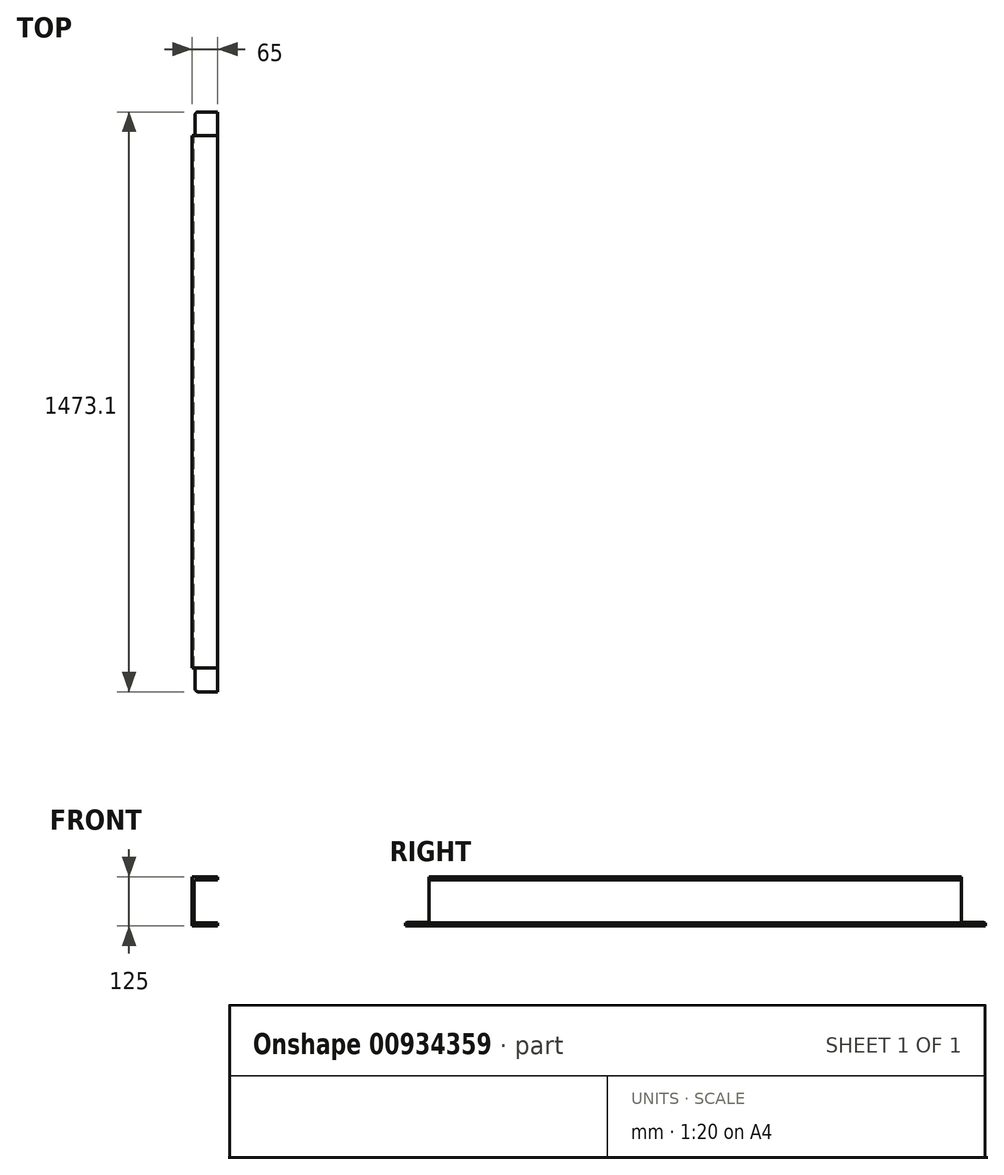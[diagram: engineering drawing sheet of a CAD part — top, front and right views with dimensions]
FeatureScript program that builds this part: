
annotation { "Feature Type Name" : "Feature", "Feature Type Description" : "" }
export const myFeature = defineFeature(function(context is Context, id is Id, definition is map)
    precondition{}
    {
        {
            var Q0;
            Q0=qCreatedBy(makeId("Front.planeOp"),FACE);
            var sketch = newSketch(context, id + "F0", { "sketchPlane" : qUnion([Q0])});
            skLineSegment(sketch, "E0", {"start": v(-25.17, -62.5) * mm, "end": v(-25.17, 62.5) * mm});
            skLineSegment(sketch, "E1", {"start": v(-25.17, 62.5) * mm, "end": v(39.83, 62.5) * mm});
            skLineSegment(sketch, "E2", {"start": v(39.83, 62.5) * mm, "end": v(39.83, 55) * mm});
            skLineSegment(sketch, "E3", {"start": v(39.83, 55) * mm, "end": v(-12.47, 55) * mm});
            skLineSegment(sketch, "E4", {"start": v(-25.17, -62.5) * mm, "end": v(39.83, -62.5) * mm});
            skLineSegment(sketch, "E5", {"start": v(39.83, -62.5) * mm, "end": v(39.83, -55) * mm});
            skLineSegment(sketch, "E6", {"start": v(39.83, -55) * mm, "end": v(-12.47, -55) * mm});
            skLineSegment(sketch, "E7", {"start": v(-20.47, -47) * mm, "end": v(-20.47, 47) * mm});
            skPoint(sketch, "E8.visualSharp", {"position": v(-20.47, 55) * mm});
            skArc(sketch, "E8.filletArc", {"start": v(-12.47, 55) * mm, "mid": v(-18.12, 52.66) * mm, "end": v(-20.47, 47) * mm});
            skPoint(sketch, "E9.visualSharp", {"position": v(-20.47, -55) * mm});
            skArc(sketch, "E9.filletArc", {"start": v(-20.47, -47) * mm, "mid": v(-18.12, -52.66) * mm, "end": v(-12.47, -55) * mm});
            skSolve(sketch);
        }
        {
            var Q0;
            Q0=makeQuery(id+"F0.imprint","IMPRINT",FACE,{"disambiguationData":[TD([[makeQuery(id+"F0.imprint","IMPRINT",EDGE,{"derivedFrom":sQuery(id+"F0.wireOp",EDGE,"E0")}),-1.0]])]});
            extrude(context, id + "F1", {"entities" : qUnion([Q0]), "depth" : 1482.5 * mm, "offsetDistance" : 25 * mm});
        }
        {
            var Q0;
            Q0=makeQuery(id+"F1.opExtrude","SWEPT_FACE",FACE,{"disambiguationData":[OSD([sQuery(id+"F0.wireOp",EDGE,"E1")])]});
            var sketch = newSketch(context, id + "F2", { "sketchPlane" : qUnion([Q0])});
            skLineSegment(sketch, "E10", {"start": v(-25.17, 0) * mm, "end": v(99.83, 0) * mm});
            skLineSegment(sketch, "E11", {"start": v(99.83, 0) * mm, "end": v(99.83, -65) * mm});
            skLineSegment(sketch, "E12", {"start": v(99.83, -65) * mm, "end": v(92.33, -65) * mm});
            skLineSegment(sketch, "E13", {"start": v(92.33, -65) * mm, "end": v(92.33, -12.7) * mm});
            skLineSegment(sketch, "E14", {"start": v(-25.17, 0) * mm, "end": v(-25.17, -65) * mm});
            skLineSegment(sketch, "E15", {"start": v(-25.17, -65) * mm, "end": v(-17.67, -65) * mm});
            skLineSegment(sketch, "E16", {"start": v(-17.67, -65) * mm, "end": v(-17.67, -12.7) * mm});
            skLineSegment(sketch, "E17", {"start": v(-9.67, -4.7) * mm, "end": v(84.33, -4.7) * mm});
            skPoint(sketch, "E18.visualSharp", {"position": v(92.33, -4.7) * mm});
            skArc(sketch, "E18.filletArc", {"start": v(92.33, -12.7) * mm, "mid": v(89.99, -7.04) * mm, "end": v(84.33, -4.7) * mm});
            skPoint(sketch, "E19.visualSharp", {"position": v(-17.67, -4.7) * mm});
            skArc(sketch, "E19.filletArc", {"start": v(-9.67, -4.7) * mm, "mid": v(-15.32, -7.04) * mm, "end": v(-17.67, -12.7) * mm});
            skLineSegment(sketch, "E20", {"start": v(99.83, -1482.5) * mm, "end": v(-25.17, -1482.5) * mm});
            skLineSegment(sketch, "E21", {"start": v(-25.17, -1482.5) * mm, "end": v(-25.17, -1417.5) * mm});
            skLineSegment(sketch, "E22", {"start": v(-25.17, -1417.5) * mm, "end": v(-17.67, -1417.5) * mm});
            skLineSegment(sketch, "E23", {"start": v(-17.67, -1417.5) * mm, "end": v(-17.67, -1469.8) * mm});
            skLineSegment(sketch, "E24", {"start": v(99.83, -1482.5) * mm, "end": v(99.83, -1417.5) * mm});
            skLineSegment(sketch, "E25", {"start": v(99.83, -1417.5) * mm, "end": v(92.33, -1417.5) * mm});
            skLineSegment(sketch, "E26", {"start": v(92.33, -1417.5) * mm, "end": v(92.33, -1469.8) * mm});
            skLineSegment(sketch, "E27", {"start": v(84.33, -1477.8) * mm, "end": v(-9.67, -1477.8) * mm});
            skPoint(sketch, "E28.visualSharp", {"position": v(-17.67, -1477.8) * mm});
            skArc(sketch, "E28.filletArc", {"start": v(-17.67, -1469.8) * mm, "mid": v(-15.32, -1475.46) * mm, "end": v(-9.67, -1477.8) * mm});
            skPoint(sketch, "E29.visualSharp", {"position": v(92.33, -1477.8) * mm});
            skArc(sketch, "E29.filletArc", {"start": v(84.33, -1477.8) * mm, "mid": v(89.99, -1475.46) * mm, "end": v(92.33, -1469.8) * mm});
            skSolve(sketch);
        }
        {
            var Q0;
            {var subQ0=sQuery(id+"F2.wireOp",EDGE,"E14");Q0=makeQuery(id+"F2.imprint","IMPRINT",FACE,{"disambiguationData":[TD([[makeQuery(id+"F2.imprint","IMPRINT",EDGE,{"derivedFrom":subQ0}),-1.0]])]});}
            var Q1;
            {var subQ5=sQuery(id+"F2.wireOp",EDGE,"E21");Q1=makeQuery(id+"F2.imprint","IMPRINT",FACE,{"disambiguationData":[TD([[makeQuery(id+"F2.imprint","IMPRINT",EDGE,{"derivedFrom":subQ5}),-1.0]])]});}
            extrude(context, id + "F3", {"entities" : qUnion([Q0, Q1]), "operationType" : NewBodyOperationType.REMOVE, "endBound" : BoundingType.THROUGH_ALL, "oppositeDirection" : true, "depth" : 25 * mm, "offsetDistance" : 25 * mm});
        }
        {
            var Q0;
            Q0=makeQuery(id+"F1.opExtrude","SWEPT_FACE",FACE,{"disambiguationData":[OSD([sQuery(id+"F0.wireOp",EDGE,"E1")])]});
            var sketch = newSketch(context, id + "F4", { "sketchPlane" : qUnion([Q0])});
            skLineSegment(sketch, "E30", {"start": v(-17.67, -1417.5) * mm, "end": v(39.83, -1417.5) * mm});
            skLineSegment(sketch, "E31", {"start": v(-17.67, -65) * mm, "end": v(39.83, -65) * mm});
            skSolve(sketch);
        }
        {
            var Q0;
            {var subQ1=sQuery(id+"F4.wireOp",EDGE,"E31");Q0=makeQuery(id+"F4.imprint","IMPRINT",FACE,{"disambiguationData":[TD([[makeQuery(id+"F4.imprint","IMPRINT",EDGE,{"derivedFrom":subQ1}),1.0]])]});}
            var Q1;
            {var subQ1=sQuery(id+"F4.wireOp",EDGE,"E30");Q1=makeQuery(id+"F4.imprint","IMPRINT",FACE,{"disambiguationData":[TD([[makeQuery(id+"F4.imprint","IMPRINT",EDGE,{"derivedFrom":subQ1}),-1.0]])]});}
            extrude(context, id + "F5", {"entities" : qUnion([Q0, Q1]), "operationType" : NewBodyOperationType.REMOVE, "oppositeDirection" : true, "depth" : 10 * mm, "offsetDistance" : 25 * mm});
        }
    });
